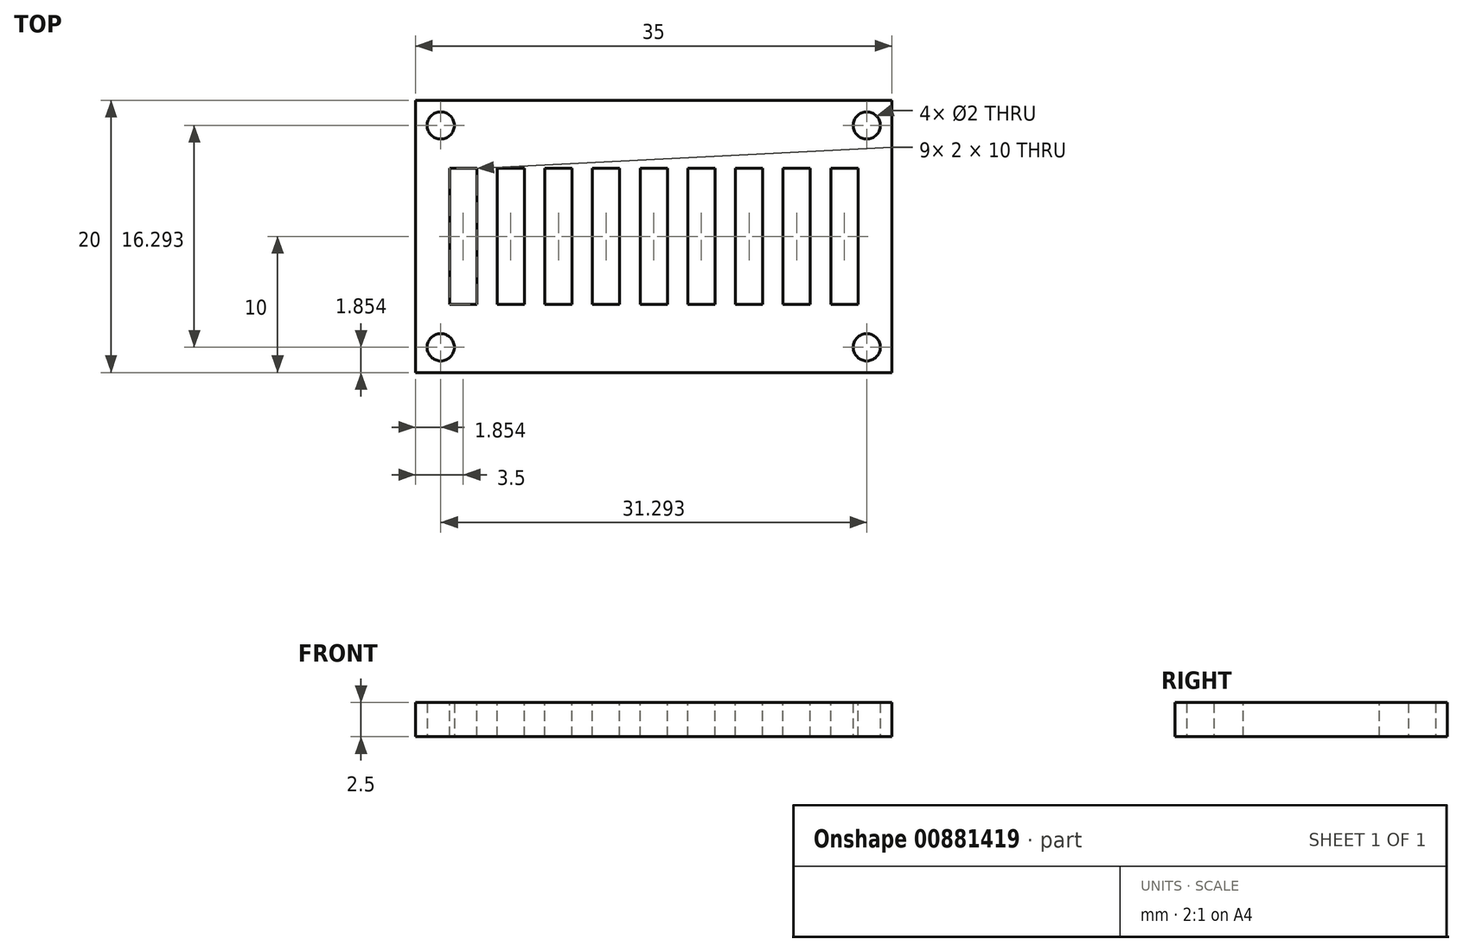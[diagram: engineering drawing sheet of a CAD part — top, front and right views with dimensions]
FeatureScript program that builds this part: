
annotation { "Feature Type Name" : "Feature", "Feature Type Description" : "" }
export const myFeature = defineFeature(function(context is Context, id is Id, definition is map)
    precondition{}
    {
        {
            var Q0;
            Q0=qCreatedBy(makeId("Top.planeOp"),FACE);
            var sketch = newSketch(context, id + "F0", { "sketchPlane" : qUnion([Q0])});
            skLineSegment(sketch, "E0.bottom", {"start": v(17.5, -10) * mm, "end": v(-17.5, -10) * mm});
            skLineSegment(sketch, "E0.top", {"start": v(17.5, 10) * mm, "end": v(-17.5, 10) * mm});
            skLineSegment(sketch, "E0.left", {"start": v(17.5, -10) * mm, "end": v(17.5, 10) * mm});
            skLineSegment(sketch, "E0.right", {"start": v(-17.5, -10) * mm, "end": v(-17.5, 10) * mm});
            skPoint(sketch, "E0.middle", {"position": v(0, 0) * mm});
            skLineSegment(sketch, "E1.0", {"start": v(-14.5, -7) * mm, "end": v(-14.5, 7) * mm});
            skLineSegment(sketch, "E1.1", {"start": v(14.5, -7) * mm, "end": v(-14.5, -7) * mm});
            skLineSegment(sketch, "E1.2", {"start": v(14.5, -7) * mm, "end": v(14.5, 7) * mm});
            skLineSegment(sketch, "E1.3", {"start": v(14.5, 7) * mm, "end": v(-14.5, 7) * mm});
            skPoint(sketch, "E2", {"position": v(14.5, 7) * mm});
            skPoint(sketch, "E3", {"position": v(17.5, 7) * mm});
            skPoint(sketch, "E4", {"position": v(14.5, 10) * mm});
            skPoint(sketch, "E5", {"position": v(-17.5, 7) * mm});
            skPoint(sketch, "E6", {"position": v(-14.5, 10) * mm});
            skPoint(sketch, "E7", {"position": v(14.5, -10) * mm});
            skPoint(sketch, "E8", {"position": v(17.5, -7) * mm});
            skPoint(sketch, "E9", {"position": v(-17.5, -7) * mm});
            skPoint(sketch, "E10", {"position": v(-14.5, -10) * mm});
            skLineSegment(sketch, "E11", {"start": v(-17.5, 7) * mm, "end": v(-14.5, 10) * mm});
            skLineSegment(sketch, "E12", {"start": v(-14.5, 7) * mm, "end": v(-17.5, 10) * mm});
            skLineSegment(sketch, "E13", {"start": v(14.5, 7) * mm, "end": v(17.5, 10) * mm});
            skLineSegment(sketch, "E14", {"start": v(17.5, 7) * mm, "end": v(14.5, 10) * mm});
            skLineSegment(sketch, "E15", {"start": v(14.5, -7) * mm, "end": v(17.5, -10) * mm});
            skLineSegment(sketch, "E16", {"start": v(14.5, -10) * mm, "end": v(17.5, -7) * mm});
            skLineSegment(sketch, "E17", {"start": v(-14.5, -10) * mm, "end": v(-17.5, -7) * mm});
            skLineSegment(sketch, "E18", {"start": v(-14.5, -7) * mm, "end": v(-17.5, -10) * mm});
            skPoint(sketch, "E19", {"position": v(-16, 8.5) * mm});
            skPoint(sketch, "E20", {"position": v(16, 8.5) * mm});
            skPoint(sketch, "E21", {"position": v(16, -8.5) * mm});
            skPoint(sketch, "E22", {"position": v(-16, -8.5) * mm});
            skPoint(sketch, "E23", {"position": v(-15.65, 8.15) * mm});
            skPoint(sketch, "E24", {"position": v(-15.65, -8.15) * mm});
            skPoint(sketch, "E25", {"position": v(15.65, -8.15) * mm});
            skPoint(sketch, "E26", {"position": v(15.65, 8.15) * mm});
            skCircle(sketch, "E27", {"center": v(15.65, -8.15) * mm, "radius": 1 * mm});
            skCircle(sketch, "E28", {"center": v(15.65, 8.15) * mm, "radius": 1 * mm});
            skCircle(sketch, "E29", {"center": v(-15.65, 8.15) * mm, "radius": 1 * mm});
            skCircle(sketch, "E30", {"center": v(-15.65, -8.15) * mm, "radius": 1 * mm});
            skSolve(sketch);
        }
        {
            var Q0;
            {var subQ1=sQuery(id+"F0.wireOp",EDGE,"E1.3");Q0=makeQuery(id+"F0.imprint","IMPRINT",FACE,{"disambiguationData":[TD([[makeQuery(id+"F0.imprint","IMPRINT",EDGE,{"derivedFrom":subQ1}),-1.0]])]});}
            var Q1;
            {var subQ10=sQuery(id+"F0.wireOp",EDGE,"E1.0");Q1=makeQuery(id+"F0.imprint","IMPRINT",FACE,{"disambiguationData":[TD([[makeQuery(id+"F0.imprint","IMPRINT",EDGE,{"derivedFrom":subQ10}),1.0]])]});}
            var Q2;
            {var subQ1=sQuery(id+"F0.wireOp",EDGE,"E0.right");var subQ3=sQuery(id+"F0.wireOp",EDGE,"E11");var subQ4=makeQuery(id+"F0.imprint","INTERSECT",VERTEX,{"derivedFrom":[subQ1,subQ3]});Q2=makeQuery(id+"F0.imprint","IMPRINT",FACE,{"disambiguationData":[TD([[makeQuery(id+"F0.imprint","IMPRINT",EDGE,{"disambiguationData":[TD([[subQ4,-1.0]])],"derivedFrom":subQ3}),1.0]])]});}
            var Q3;
            {var subQ1=sQuery(id+"F0.wireOp",EDGE,"E0.top");var subQ3=sQuery(id+"F0.wireOp",EDGE,"E11");var subQ4=makeQuery(id+"F0.imprint","INTERSECT",VERTEX,{"derivedFrom":[subQ1,subQ3]});Q3=makeQuery(id+"F0.imprint","IMPRINT",FACE,{"disambiguationData":[TD([[makeQuery(id+"F0.imprint","IMPRINT",EDGE,{"disambiguationData":[TD([[subQ4,1.0]])],"derivedFrom":subQ3}),1.0]])]});}
            var Q4;
            Q4=makeQuery(id+"F0.imprint","IMPRINT",FACE,{"disambiguationData":[TD([[makeQuery(id+"F0.imprint","IMPRINT",EDGE,{"derivedFrom":sQuery(id+"F0.wireOp",EDGE,"E1.0")}),-1.0]])]});
            var Q5;
            {var subQ1=sQuery(id+"F0.wireOp",EDGE,"E0.left");var subQ3=sQuery(id+"F0.wireOp",EDGE,"E14");var subQ4=makeQuery(id+"F0.imprint","INTERSECT",VERTEX,{"derivedFrom":[subQ1,subQ3]});Q5=makeQuery(id+"F0.imprint","IMPRINT",FACE,{"disambiguationData":[TD([[makeQuery(id+"F0.imprint","IMPRINT",EDGE,{"disambiguationData":[TD([[subQ4,-1.0]])],"derivedFrom":subQ3}),-1.0]])]});}
            var Q6;
            {var subQ1=sQuery(id+"F0.wireOp",EDGE,"E0.top");var subQ3=sQuery(id+"F0.wireOp",EDGE,"E14");var subQ4=makeQuery(id+"F0.imprint","INTERSECT",VERTEX,{"derivedFrom":[subQ1,subQ3]});Q6=makeQuery(id+"F0.imprint","IMPRINT",FACE,{"disambiguationData":[TD([[makeQuery(id+"F0.imprint","IMPRINT",EDGE,{"disambiguationData":[TD([[subQ4,1.0]])],"derivedFrom":subQ3}),-1.0]])]});}
            var Q7;
            {var subQ10=sQuery(id+"F0.wireOp",EDGE,"E1.2");Q7=makeQuery(id+"F0.imprint","IMPRINT",FACE,{"disambiguationData":[TD([[makeQuery(id+"F0.imprint","IMPRINT",EDGE,{"derivedFrom":subQ10}),-1.0]])]});}
            var Q8;
            {var subQ1=sQuery(id+"F0.wireOp",EDGE,"E0.bottom");var subQ3=sQuery(id+"F0.wireOp",EDGE,"E16");var subQ4=makeQuery(id+"F0.imprint","INTERSECT",VERTEX,{"derivedFrom":[subQ1,subQ3]});Q8=makeQuery(id+"F0.imprint","IMPRINT",FACE,{"disambiguationData":[TD([[makeQuery(id+"F0.imprint","IMPRINT",EDGE,{"disambiguationData":[TD([[subQ4,-1.0]])],"derivedFrom":subQ3}),-1.0]])]});}
            var Q9;
            {var subQ1=sQuery(id+"F0.wireOp",EDGE,"E0.left");var subQ3=sQuery(id+"F0.wireOp",EDGE,"E16");var subQ4=makeQuery(id+"F0.imprint","INTERSECT",VERTEX,{"derivedFrom":[subQ1,subQ3]});Q9=makeQuery(id+"F0.imprint","IMPRINT",FACE,{"disambiguationData":[TD([[makeQuery(id+"F0.imprint","IMPRINT",EDGE,{"disambiguationData":[TD([[subQ4,1.0]])],"derivedFrom":subQ3}),-1.0]])]});}
            var Q10;
            {var subQ1=sQuery(id+"F0.wireOp",EDGE,"E1.1");Q10=makeQuery(id+"F0.imprint","IMPRINT",FACE,{"disambiguationData":[TD([[makeQuery(id+"F0.imprint","IMPRINT",EDGE,{"derivedFrom":subQ1}),1.0]])]});}
            var Q11;
            {var subQ1=sQuery(id+"F0.wireOp",EDGE,"E0.bottom");var subQ3=sQuery(id+"F0.wireOp",EDGE,"E17");var subQ4=makeQuery(id+"F0.imprint","INTERSECT",VERTEX,{"derivedFrom":[subQ1,subQ3]});Q11=makeQuery(id+"F0.imprint","IMPRINT",FACE,{"disambiguationData":[TD([[makeQuery(id+"F0.imprint","IMPRINT",EDGE,{"disambiguationData":[TD([[subQ4,-1.0]])],"derivedFrom":subQ3}),1.0]])]});}
            var Q12;
            {var subQ1=sQuery(id+"F0.wireOp",EDGE,"E0.right");var subQ3=sQuery(id+"F0.wireOp",EDGE,"E17");var subQ4=makeQuery(id+"F0.imprint","INTERSECT",VERTEX,{"derivedFrom":[subQ1,subQ3]});Q12=makeQuery(id+"F0.imprint","IMPRINT",FACE,{"disambiguationData":[TD([[makeQuery(id+"F0.imprint","IMPRINT",EDGE,{"disambiguationData":[TD([[subQ4,1.0]])],"derivedFrom":subQ3}),1.0]])]});}
            extrude(context, id + "F1", {"entities" : qUnion([Q0, Q1, Q2, Q3, Q4, Q5, Q6, Q7, Q8, Q9, Q10, Q11, Q12]), "depth" : 2.5 * mm, "offsetDistance" : 25 * mm});
        }
        {
            var Q0;
            Q0=makeQuery(id+"F1.opExtrude","CAP_FACE",FACE,{"disambiguationData":[OSD([sQuery(id+"F0.wireOp",EDGE,"E0.bottom"),sQuery(id+"F0.wireOp",EDGE,"E0.top"),sQuery(id+"F0.wireOp",EDGE,"E0.left"),sQuery(id+"F0.wireOp",EDGE,"E0.right"),sQuery(id+"F0.wireOp",EDGE,"eZebsT4n-WIH0-X7CC-yJz8-MYBLBg1WA7Y4"),sQuery(id+"F0.wireOp",EDGE,"c4W0w5mN-MFB0-S6FC-HKoJ-5AvOucdbbtQr"),sQuery(id+"F0.wireOp",EDGE,"K5nXyZFh-V7nY-kMfR-U5du-vQeuOazLRvFL"),sQuery(id+"F0.wireOp",EDGE,"BXerWKJc-SouJ-FrdJ-XHRB-KdtjOES64cUG")])],"isStart":false});
            var sketch = newSketch(context, id + "F2", { "sketchPlane" : qUnion([Q0])});
            skPoint(sketch, "E31", {"position": v(0, 0) * mm});
            skPoint(sketch, "E32", {"position": v(-3.5, 0) * mm});
            skPoint(sketch, "E33", {"position": v(-7, 0) * mm});
            skPoint(sketch, "E34", {"position": v(-10.5, 0) * mm});
            skPoint(sketch, "E35", {"position": v(-14, 0) * mm});
            skPoint(sketch, "E36", {"position": v(3.5, 0) * mm});
            skPoint(sketch, "E37", {"position": v(7, 0) * mm});
            skPoint(sketch, "E38", {"position": v(10.5, 0) * mm});
            skPoint(sketch, "E39", {"position": v(14, 0) * mm});
            skLineSegment(sketch, "E40.bottom", {"start": v(-13, -5) * mm, "end": v(-15, -5) * mm});
            skLineSegment(sketch, "E40.top", {"start": v(-13, 5) * mm, "end": v(-15, 5) * mm});
            skLineSegment(sketch, "E40.left", {"start": v(-13, -5) * mm, "end": v(-13, 5) * mm});
            skLineSegment(sketch, "E40.right", {"start": v(-15, -5) * mm, "end": v(-15, 5) * mm});
            skLineSegment(sketch, "E41.bottom", {"start": v(-9.5, -5) * mm, "end": v(-11.5, -5) * mm});
            skLineSegment(sketch, "E41.top", {"start": v(-9.5, 5) * mm, "end": v(-11.5, 5) * mm});
            skLineSegment(sketch, "E41.left", {"start": v(-9.5, -5) * mm, "end": v(-9.5, 5) * mm});
            skLineSegment(sketch, "E41.right", {"start": v(-11.5, -5) * mm, "end": v(-11.5, 5) * mm});
            skPoint(sketch, "E41.cornerSnap0", {"position": v(-14, -5) * mm});
            skLineSegment(sketch, "E42.bottom", {"start": v(-6, -5) * mm, "end": v(-8, -5) * mm});
            skLineSegment(sketch, "E42.top", {"start": v(-6, 5) * mm, "end": v(-8, 5) * mm});
            skLineSegment(sketch, "E42.left", {"start": v(-6, -5) * mm, "end": v(-6, 5) * mm});
            skLineSegment(sketch, "E42.right", {"start": v(-8, -5) * mm, "end": v(-8, 5) * mm});
            skLineSegment(sketch, "E43.bottom", {"start": v(-4.5, -5) * mm, "end": v(-2.5, -5) * mm});
            skLineSegment(sketch, "E43.top", {"start": v(-4.5, 5) * mm, "end": v(-2.5, 5) * mm});
            skLineSegment(sketch, "E43.left", {"start": v(-4.5, -5) * mm, "end": v(-4.5, 5) * mm});
            skLineSegment(sketch, "E43.right", {"start": v(-2.5, -5) * mm, "end": v(-2.5, 5) * mm});
            skLineSegment(sketch, "E44.bottom", {"start": v(-1, -5) * mm, "end": v(1, -5) * mm});
            skLineSegment(sketch, "E44.top", {"start": v(-1, 5) * mm, "end": v(1, 5) * mm});
            skLineSegment(sketch, "E44.left", {"start": v(-1, -5) * mm, "end": v(-1, 5) * mm});
            skLineSegment(sketch, "E44.right", {"start": v(1, -5) * mm, "end": v(1, 5) * mm});
            skLineSegment(sketch, "E45.bottom", {"start": v(2.5, -5) * mm, "end": v(4.5, -5) * mm});
            skLineSegment(sketch, "E45.top", {"start": v(2.5, 5) * mm, "end": v(4.5, 5) * mm});
            skLineSegment(sketch, "E45.left", {"start": v(2.5, -5) * mm, "end": v(2.5, 5) * mm});
            skLineSegment(sketch, "E45.right", {"start": v(4.5, -5) * mm, "end": v(4.5, 5) * mm});
            skLineSegment(sketch, "E46.bottom", {"start": v(8, -5) * mm, "end": v(6, -5) * mm});
            skLineSegment(sketch, "E46.top", {"start": v(8, 5) * mm, "end": v(6, 5) * mm});
            skLineSegment(sketch, "E46.left", {"start": v(8, -5) * mm, "end": v(8, 5) * mm});
            skLineSegment(sketch, "E46.right", {"start": v(6, -5) * mm, "end": v(6, 5) * mm});
            skLineSegment(sketch, "E47.bottom", {"start": v(11.5, -5) * mm, "end": v(9.5, -5) * mm});
            skLineSegment(sketch, "E47.top", {"start": v(11.5, 5) * mm, "end": v(9.5, 5) * mm});
            skLineSegment(sketch, "E47.left", {"start": v(11.5, -5) * mm, "end": v(11.5, 5) * mm});
            skLineSegment(sketch, "E47.right", {"start": v(9.5, -5) * mm, "end": v(9.5, 5) * mm});
            skLineSegment(sketch, "E48.bottom", {"start": v(15, -5) * mm, "end": v(13, -5) * mm});
            skLineSegment(sketch, "E48.top", {"start": v(15, 5) * mm, "end": v(13, 5) * mm});
            skLineSegment(sketch, "E48.left", {"start": v(15, -5) * mm, "end": v(15, 5) * mm});
            skLineSegment(sketch, "E48.right", {"start": v(13, -5) * mm, "end": v(13, 5) * mm});
            skSolve(sketch);
        }
        {
            var Q0;
            Q0=makeQuery(id+"F2.imprint","IMPRINT",FACE,{"disambiguationData":[TD([[makeQuery(id+"F2.imprint","IMPRINT",EDGE,{"derivedFrom":sQuery(id+"F2.wireOp",EDGE,"E40.bottom")}),-1.0]])]});
            var Q1;
            Q1=makeQuery(id+"F2.imprint","IMPRINT",FACE,{"disambiguationData":[TD([[makeQuery(id+"F2.imprint","IMPRINT",EDGE,{"derivedFrom":sQuery(id+"F2.wireOp",EDGE,"E41.bottom")}),-1.0]])]});
            var Q2;
            Q2=makeQuery(id+"F2.imprint","IMPRINT",FACE,{"disambiguationData":[TD([[makeQuery(id+"F2.imprint","IMPRINT",EDGE,{"derivedFrom":sQuery(id+"F2.wireOp",EDGE,"E42.bottom")}),-1.0]])]});
            var Q3;
            Q3=makeQuery(id+"F2.imprint","IMPRINT",FACE,{"disambiguationData":[TD([[makeQuery(id+"F2.imprint","IMPRINT",EDGE,{"derivedFrom":sQuery(id+"F2.wireOp",EDGE,"E43.bottom")}),1.0]])]});
            var Q4;
            Q4=makeQuery(id+"F2.imprint","IMPRINT",FACE,{"disambiguationData":[TD([[makeQuery(id+"F2.imprint","IMPRINT",EDGE,{"derivedFrom":sQuery(id+"F2.wireOp",EDGE,"E44.bottom")}),1.0]])]});
            var Q5;
            Q5=makeQuery(id+"F2.imprint","IMPRINT",FACE,{"disambiguationData":[TD([[makeQuery(id+"F2.imprint","IMPRINT",EDGE,{"derivedFrom":sQuery(id+"F2.wireOp",EDGE,"E45.bottom")}),1.0]])]});
            var Q6;
            Q6=makeQuery(id+"F2.imprint","IMPRINT",FACE,{"disambiguationData":[TD([[makeQuery(id+"F2.imprint","IMPRINT",EDGE,{"derivedFrom":sQuery(id+"F2.wireOp",EDGE,"E46.bottom")}),-1.0]])]});
            var Q7;
            Q7=makeQuery(id+"F2.imprint","IMPRINT",FACE,{"disambiguationData":[TD([[makeQuery(id+"F2.imprint","IMPRINT",EDGE,{"derivedFrom":sQuery(id+"F2.wireOp",EDGE,"E47.bottom")}),-1.0]])]});
            var Q8;
            Q8=makeQuery(id+"F2.imprint","IMPRINT",FACE,{"disambiguationData":[TD([[makeQuery(id+"F2.imprint","IMPRINT",EDGE,{"derivedFrom":sQuery(id+"F2.wireOp",EDGE,"E48.bottom")}),-1.0]])]});
            extrude(context, id + "F3", {"entities" : qUnion([Q0, Q1, Q2, Q3, Q4, Q5, Q6, Q7, Q8]), "operationType" : NewBodyOperationType.REMOVE, "oppositeDirection" : true, "depth" : 25 * mm, "offsetDistance" : 25 * mm});
        }
    });
